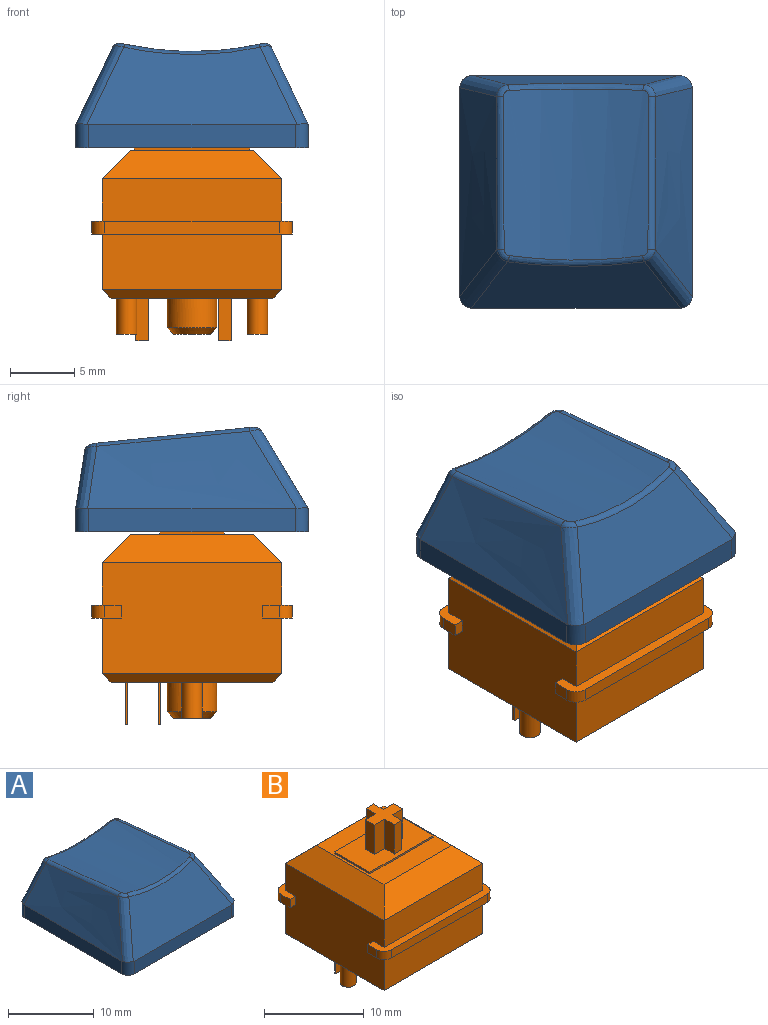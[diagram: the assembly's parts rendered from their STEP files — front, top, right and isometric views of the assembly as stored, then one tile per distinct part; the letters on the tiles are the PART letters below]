
ASSEMBLY  parts=2 mates=1
PART A: 50 faces, bbox 21.2x21.9x10.6 mm
  f0: plane 18.1x18.1mm, normal (0,0,-1), area 67.5mm2, adj f1,f2,f3,f4,f10,f12,f14,f16
  f1: plane 16.1x1.8mm, normal (1,0,0), area 29mm2, adj f0,f8,f10,f16
  f2: plane 16.1x1.8mm, normal (0,1,0), area 29mm2, adj f0,f5,f14,f15,f16,f17
  f3: plane 16.1x1.8mm, normal (-1,0,0), area 29mm2, adj f0,f6,f12,f14
  f4: plane 16.1x1.8mm, normal (0,-1,0), area 29mm2, adj f0,f7,f10,f12
  f5: plane 15.96x4.53mm, normal (0,0.99,0.15), area 56.4mm2, adj f2,f15,f17,f20
  f6: bspline ~18.1x6.49mm, area 87.4mm2, adj f3,f12,f13,f14,f15,f19
  f7: plane 16.37x6.05mm, normal (0,-0.86,0.51), area 90.2mm2, adj f4,f10,f11,f12,f13,f23
  f8: bspline ~18.1x6.49mm, area 87.4mm2, adj f1,f10,f11,f16,f17,f24
  f9: cylinder r=22.9mm len=12.94mm, axis (0,0.99,-0.1), area 146.4mm2, adj f18,f19,f20,f21,f22,f23,f24,f25
  f10: cylinder r=1mm len=1.88mm, axis (0,0,-1), area 2.9mm2, adj f0,f1,f4,f7,f8,f11
  f11: bspline ~7.99x5.46mm, area 10.4mm2, adj f7,f8,f10,f25
  f12: cylinder r=1mm len=1.88mm, axis (0,0,1), area 2.9mm2, adj f0,f3,f4,f6,f7,f13
  f13: bspline ~8.01x5.47mm, area 10.4mm2, adj f6,f7,f12,f21
  f14: cylinder r=1mm len=1.8mm, axis (0,0,-1), area 2.8mm2, adj f0,f2,f3,f6,f15
  f15: bspline ~6.46x4.4mm, area 8.2mm2, adj f2,f5,f6,f14,f18
  f16: cylinder r=1mm len=1.8mm, axis (0,0,1), area 2.8mm2, adj f0,f1,f2,f8,f17
  f17: bspline ~6.45x4.39mm, area 8.2mm2, adj f2,f5,f8,f16,f22
  f18: bspline ~1.17x1.02mm, area 0.7mm2, adj f9,f15,f19,f20
  f19: bspline ~17.37x2.1mm, area 8mm2, adj f6,f9,f18,f21
  f20: bspline ~10.64x1.03mm, area 7mm2, adj f5,f9,f18,f22
  f21: bspline ~1.13x1.07mm, area 0.7mm2, adj f9,f13,f19,f23
  f22: bspline ~1.17x1mm, area 0.7mm2, adj f9,f17,f20,f24
  f23: bspline ~10.62x0.82mm, area 6mm2, adj f7,f9,f21,f25
  f24: bspline ~17.37x2.1mm, area 8mm2, adj f8,f9,f22,f25
  f25: bspline ~1.24x1.01mm, area 0.7mm2, adj f9,f11,f23,f24
  f26: plane 16.13x1.61mm, normal (-1,0,0), area 25mm2, adj f0,f27,f29,f32,f33
  f27: plane 16.1x1.72mm, normal (0,-1,0), area 27.7mm2, adj f0,f26,f28,f30,f31,f33
  f28: plane 16.13x1.61mm, normal (1,0,0), area 25mm2, adj f0,f27,f29,f31,f32
  f29: plane 16.1x1.52mm, normal (0,1,0), area 24.5mm2, adj f0,f26,f28,f32
  f30: plane 16.21x4.45mm, normal (0,-0.99,-0.15), area 51mm2, adj f27,f31,f33,f34
  f31: offset ~20.1x8.49mm, area 78.8mm2, adj f27,f28,f30,f32,f34
  f32: plane 16.68x6.12mm, normal (0,0.86,-0.51), area 82.2mm2, adj f26,f28,f29,f31,f33,f34
  f33: offset ~20.1x8.49mm, area 78.8mm2, adj f26,f27,f30,f32,f34
  f34: cylinder r=23.9mm len=12.22mm, axis (0,0.99,-0.1), area 111.1mm2, adj f30,f31,f32,f33,f46
  f35: plane 5.88x1.35mm, normal (-1,0,0), area 7.8mm2, adj f36,f44,f45,f49
  f36: plane 5.97x1.5mm, normal (0,-1,0), area 8.9mm2, adj f35,f37,f45,f49
  f37: plane 6.1x1.3mm, normal (-1,0,0), area 7.8mm2, adj f36,f38,f45,f49
  f38: plane 6.1x1.5mm, normal (0,1,0), area 9.1mm2, adj f37,f39,f45,f49
  f39: plane 6.16x1.35mm, normal (-1,0,0), area 8.2mm2, adj f38,f40,f45,f49
  f40: plane 6.16x1mm, normal (0,1,0), area 6.2mm2, adj f39,f41,f45,f49
  f41: plane 6.16x1.35mm, normal (1,0,0), area 8.2mm2, adj f40,f42,f45,f49
  f42: plane 6.1x1.5mm, normal (0,1,0), area 9.1mm2, adj f41,f43,f45,f49
  f43: plane 6.1x1.3mm, normal (1,0,0), area 7.8mm2, adj f42,f45,f47,f49
  f44: plane 5.74x1mm, normal (0,-1,0), area 5.7mm2, adj f35,f45,f48,f49
  f45: plane 5.5x5.5mm, normal (0,0,-1), area 15.9mm2, adj f35,f36,f37,f38,f39,f40,f41,f42
  f46: cylinder r=2.75mm len=6.11mm, axis (0,0,-1), area 105.5mm2, adj f34,f45
  f47: plane 5.97x1.5mm, normal (0,-1,0), area 8.9mm2, adj f43,f45,f48,f49
  f48: plane 5.88x1.35mm, normal (1,0,0), area 7.8mm2, adj f44,f45,f47,f49
  f49: cylinder r=23.9mm len=4.01mm, axis (0,0.99,-0.1), area 7.9mm2, adj f35,f36,f37,f38,f39,f40,f41,f42
PART B: 69 faces, bbox 15.6x15.6x18.6 mm
  f0: plane 15.6x2.3mm, normal (0,0,-1), area 14.4mm2, adj f2,f3,f28,f30,f35,f60,f62,f63
  f1: plane 15.6x2.3mm, normal (0,0,-1), area 14.4mm2, adj f28,f30,f33,f34,f36,f59,f61,f64
  f2: plane 1.3x1mm, normal (1,0,0), area 1.3mm2, adj f0,f32,f62,f66
  f3: plane 1.3x1mm, normal (-1,0,0), area 1.3mm2, adj f0,f32,f63,f68
  f4: plane 15.6x2.3mm, normal (0,0,1), area 14.4mm2, adj f28,f30,f31,f33,f34,f36,f61,f64
  f5: plane 14x2.2mm, normal (-0.71,0,0.71), area 36.7mm2, adj f6,f7,f26,f30
  f6: plane 14x2.2mm, normal (0,-0.71,0.71), area 36.7mm2, adj f5,f7,f27,f31
  f7: plane 9.6x9.6mm, normal (0,0,1), area 47.2mm2, adj f5,f6,f8,f9,f10,f11,f26,f27
  f8: plane 5x0.2mm, normal (1,0,0), area 1mm2, adj f7,f9,f11,f12
  f9: plane 9x0.2mm, normal (0,1,0), area 1.8mm2, adj f7,f8,f10,f12
  f10: plane 5x0.2mm, normal (-1,0,0), area 1mm2, adj f7,f9,f11,f12
  f11: plane 9x0.2mm, normal (0,-1,0), area 1.8mm2, adj f7,f8,f10,f12
  f12: plane 9x5mm, normal (0,0,1), area 36.9mm2, adj f8,f9,f10,f11,f13,f14,f15,f16
  f13: plane 3.6x1.35mm, normal (1,0,0), area 4.9mm2, adj f12,f14,f24,f25
  f14: plane 3.6x1.08mm, normal (0,1,0), area 3.9mm2, adj f12,f13,f15,f25
  f15: plane 3.6x1.35mm, normal (-1,0,0), area 4.9mm2, adj f12,f14,f16,f25
  f16: plane 3.6x1.46mm, normal (0,1,0), area 5.3mm2, adj f12,f15,f17,f25
  f17: plane 3.6x1.3mm, normal (-1,0,0), area 4.7mm2, adj f12,f16,f18,f25
  f18: plane 3.6x1.46mm, normal (0,-1,0), area 5.3mm2, adj f12,f17,f19,f25
  f19: plane 3.6x1.35mm, normal (-1,0,0), area 4.9mm2, adj f12,f18,f20,f25
  f20: plane 3.6x1.08mm, normal (0,-1,0), area 3.9mm2, adj f12,f19,f21,f25
  f21: plane 3.6x1.35mm, normal (1,0,0), area 4.9mm2, adj f12,f20,f22,f25
  f22: plane 3.6x1.46mm, normal (0,-1,0), area 5.3mm2, adj f12,f21,f23,f25
  f23: plane 3.6x1.3mm, normal (1,0,0), area 4.7mm2, adj f12,f22,f24,f25
  f24: plane 3.6x1.46mm, normal (0,1,0), area 5.3mm2, adj f12,f13,f23,f25
  f25: plane 4x4mm, normal (0,0,1), area 8.1mm2, adj f13,f14,f15,f16,f17,f18,f19,f20
  f26: plane 14x2.2mm, normal (0,0.71,0.71), area 36.7mm2, adj f5,f7,f27,f29
  f27: plane 14x2.2mm, normal (0.71,0,0.71), area 36.7mm2, adj f6,f7,f26,f28
  f28: plane 14x8.6mm, normal (1,0,0), area 117.4mm2, adj f0,f1,f4,f27,f29,f31,f32,f55
  f29: plane 14x3.3mm, normal (0,1,0), area 46.2mm2, adj f26,f28,f30,f32
  f30: plane 14x8.6mm, normal (-1,0,0), area 117.4mm2, adj f0,f1,f4,f5,f29,f31,f32,f57
  f31: plane 14x3.3mm, normal (0,-1,0), area 46.2mm2, adj f4,f6,f28,f30
  f32: plane 15.6x2.3mm, normal (0,0,1), area 14.4mm2, adj f2,f3,f28,f29,f30,f35,f62,f63
  f33: plane 13.6x1mm, normal (0,-1,0), area 13.6mm2, adj f1,f4,f61,f64
  f34: plane 1.3x1mm, normal (1,0,0), area 1.3mm2, adj f1,f4,f61,f65
  f35: plane 13.6x1mm, normal (0,1,0), area 13.6mm2, adj f0,f32,f62,f63
  f36: plane 1.3x1mm, normal (-1,0,0), area 1.3mm2, adj f1,f4,f64,f67
  f37: plane 2.85x2.85mm, normal (0,0,-1), area 6.4mm2, adj f38
  f38: cone r=1.43mm half-angle=45deg, axis (0,0,1), area 7.4mm2, adj f37,f43
  f39: plane 1x0.2mm, normal (0,0,-1), area 0.2mm2, adj f44,f45,f46,f47
  f40: plane 1x0.2mm, normal (0,0,-1), area 0.2mm2, adj f48,f49,f50,f51
  f41: plane 1.6x1.6mm, normal (0,0,-1), area 2mm2, adj f52
  f42: plane 1.6x1.6mm, normal (0,0,-1), area 2mm2, adj f53
  f43: cylinder r=1.93mm len=3.85mm, axis (0,0,1), area 27.8mm2, adj f38,f54
  f44: plane 3.3x0.2mm, normal (-1,0,0), area 0.7mm2, adj f39,f45,f47,f54
  f45: plane 3.3x1mm, normal (0,1,0), area 3.3mm2, adj f39,f44,f46,f54
  f46: plane 3.3x0.2mm, normal (1,0,0), area 0.7mm2, adj f39,f45,f47,f54
  f47: plane 3.3x1mm, normal (0,-1,0), area 3.3mm2, adj f39,f44,f46,f54
  f48: plane 3.3x0.2mm, normal (-1,0,0), area 0.7mm2, adj f40,f49,f51,f54
  f49: plane 3.3x1mm, normal (0,1,0), area 3.3mm2, adj f40,f48,f50,f54
  f50: plane 3.3x0.2mm, normal (1,0,0), area 0.7mm2, adj f40,f49,f51,f54
  f51: plane 3.3x1mm, normal (0,-1,0), area 3.3mm2, adj f40,f48,f50,f54
  f52: cylinder r=0.8mm len=2.8mm, axis (0,0,1), area 14.1mm2, adj f41,f54
  f53: cylinder r=0.8mm len=2.8mm, axis (0,0,1), area 14.1mm2, adj f42,f54
  f54: plane 12.6x12.6mm, normal (0,0,-1), area 142.7mm2, adj f43,f44,f45,f46,f47,f48,f49,f50
  f55: plane 14x0.7mm, normal (0.71,0,-0.71), area 13.2mm2, adj f28,f54,f56,f58
  f56: plane 14x0.7mm, normal (0,0.71,-0.71), area 13.2mm2, adj f54,f55,f57,f60
  f57: plane 14x0.7mm, normal (-0.71,0,-0.71), area 13.2mm2, adj f30,f54,f56,f58
  f58: plane 14x0.7mm, normal (0,-0.71,-0.71), area 13.2mm2, adj f54,f55,f57,f59
  f59: plane 14x4.3mm, normal (0,-1,0), area 60.2mm2, adj f1,f28,f30,f58
  f60: plane 14x4.3mm, normal (0,1,0), area 60.2mm2, adj f0,f28,f30,f56
  f61: cylinder r=1mm len=1mm, axis (0,0,-1), area 1.6mm2, adj f1,f4,f33,f34
  f62: cylinder r=1mm len=1mm, axis (0,0,1), area 1.6mm2, adj f0,f2,f32,f35
  f63: cylinder r=1mm len=1mm, axis (0,0,-1), area 1.6mm2, adj f0,f3,f32,f35
  f64: cylinder r=1mm len=1mm, axis (0,0,1), area 1.6mm2, adj f1,f4,f33,f36
  f65: plane 1x0.8mm, normal (0,1,0), area 0.8mm2, adj f1,f4,f28,f34
  f66: plane 1x0.8mm, normal (0,-1,0), area 0.8mm2, adj f0,f2,f28,f32
  f67: plane 1x0.8mm, normal (0,1,0), area 0.8mm2, adj f1,f4,f30,f36
  f68: plane 1x0.8mm, normal (0,-1,0), area 0.8mm2, adj f0,f3,f30,f32
PLACE A t=(0,0,11.7)mm
PLACE B at identity fixed
MATE fastened B.f38 <-> A.f46  axis (0,0,1) through (0,0,11.7)mm
